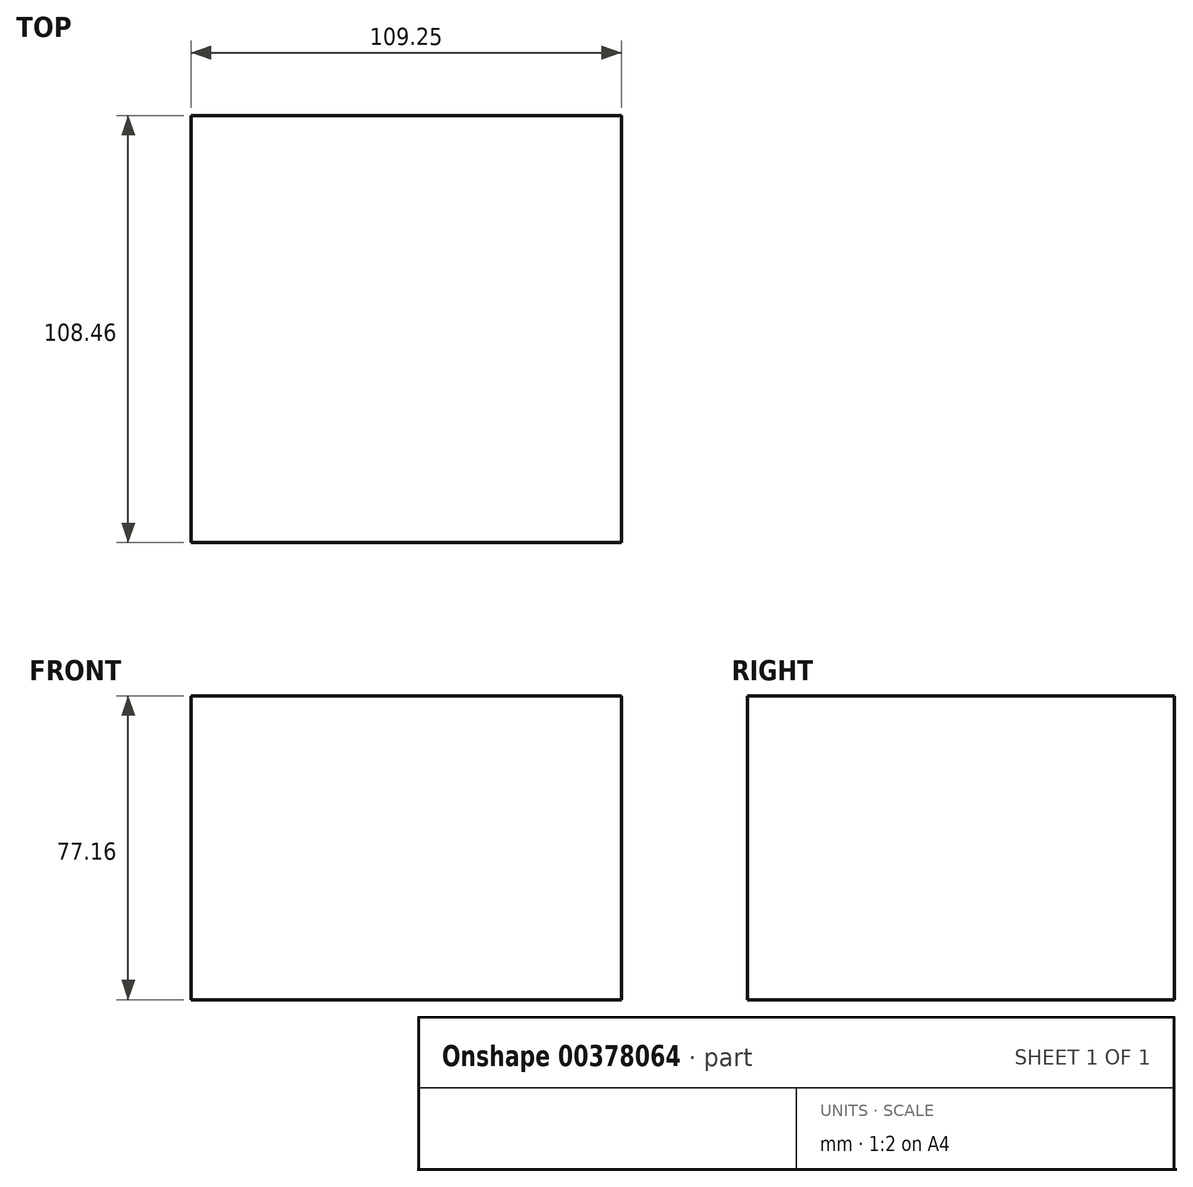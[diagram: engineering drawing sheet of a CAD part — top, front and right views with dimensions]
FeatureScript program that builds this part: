
annotation { "Feature Type Name" : "Feature", "Feature Type Description" : "" }
export const myFeature = defineFeature(function(context is Context, id is Id, definition is map)
    precondition{}
    {
        {
            var Q0;
            Q0=qCreatedBy(makeId("Front.planeOp"),FACE);
            var sketch = newSketch(context, id + "F0", { "sketchPlane" : qUnion([Q0])});
            skLineSegment(sketch, "E0.bottom", {"start": v(-115.8, 53.42) * mm, "end": v(-6.55, 53.42) * mm});
            skLineSegment(sketch, "E0.top", {"start": v(-115.8, -23.74) * mm, "end": v(-6.55, -23.74) * mm});
            skLineSegment(sketch, "E0.left", {"start": v(-115.8, 53.42) * mm, "end": v(-115.8, -23.74) * mm});
            skLineSegment(sketch, "E0.right", {"start": v(-6.55, 53.42) * mm, "end": v(-6.55, -23.74) * mm});
            skSolve(sketch);
        }
        {
            var Q0;
            Q0=makeQuery(id+"F0.imprint","IMPRINT",FACE,{"disambiguationData":[TD([[makeQuery(id+"F0.imprint","IMPRINT",EDGE,{"derivedFrom":sQuery(id+"F0.wireOp",EDGE,"E0.bottom")}),-1.0]])]});
            extrude(context, id + "F1", {"entities" : qUnion([Q0]), "depth" : 108.46 * mm});
        }
    });
